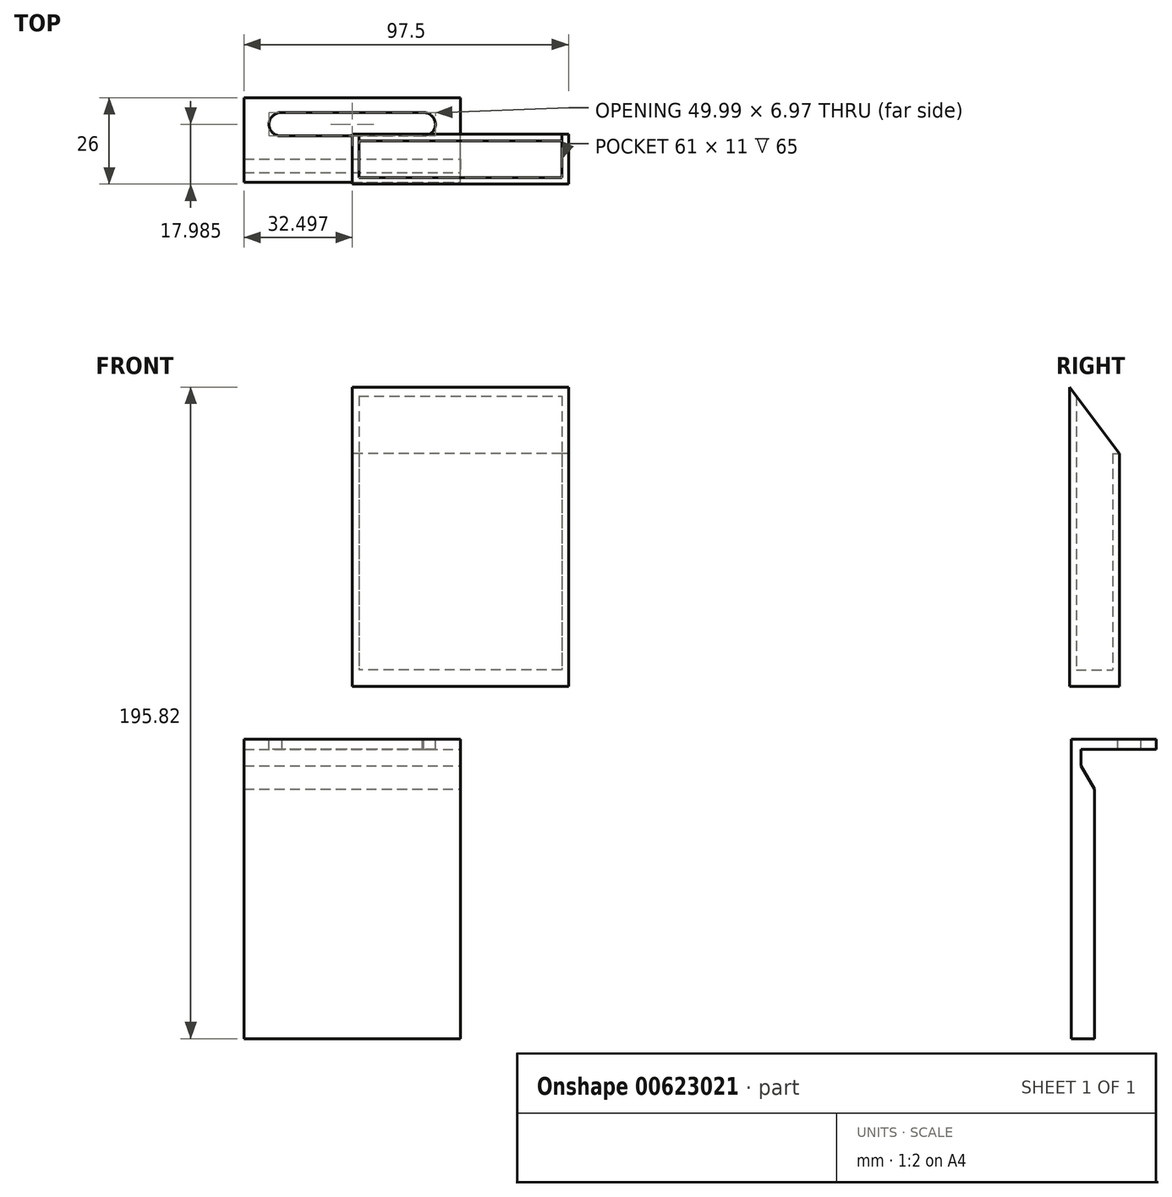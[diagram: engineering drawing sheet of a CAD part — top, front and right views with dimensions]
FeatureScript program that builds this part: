
annotation { "Feature Type Name" : "Feature", "Feature Type Description" : "" }
export const myFeature = defineFeature(function(context is Context, id is Id, definition is map)
    precondition{}
    {
        {
            var Q0;
            Q0=qCreatedBy(makeId("Top.planeOp"),FACE);
            var sketch = newSketch(context, id + "F0", { "sketchPlane" : qUnion([Q0])});
            skLineSegment(sketch, "E0.bottom", {"start": v(32.5, -7.5) * mm, "end": v(-32.5, -7.5) * mm});
            skLineSegment(sketch, "E0.top", {"start": v(32.5, 7.5) * mm, "end": v(-32.5, 7.5) * mm});
            skLineSegment(sketch, "E0.left", {"start": v(32.5, -7.5) * mm, "end": v(32.5, 7.5) * mm});
            skLineSegment(sketch, "E0.right", {"start": v(-32.5, -7.5) * mm, "end": v(-32.5, 7.5) * mm});
            skPoint(sketch, "E0.middle", {"position": v(0, 0) * mm});
            skSolve(sketch);
        }
        {
            var Q0;
            Q0 = qSketchRegion(id + "F0", true);
            extrude(context, id + "F1", {"entities" : qUnion([Q0]), "depth" : 5 * mm, "offsetDistance" : 25 * mm});
        }
        {
            var Q0;
            Q0=makeQuery(id+"F1.opExtrude","CAP_FACE",FACE,{"disambiguationData":[OSD([sQuery(id+"F0.wireOp",EDGE,"E0.bottom"),sQuery(id+"F0.wireOp",EDGE,"E0.top"),sQuery(id+"F0.wireOp",EDGE,"E0.left"),sQuery(id+"F0.wireOp",EDGE,"E0.right")])],"isStart":false});
            var sketch = newSketch(context, id + "F2", { "sketchPlane" : qUnion([Q0])});
            skLineSegment(sketch, "E1.bottom", {"start": v(32.5, -7.5) * mm, "end": v(-32.5, -7.5) * mm});
            skLineSegment(sketch, "E1.top", {"start": v(32.5, 7.5) * mm, "end": v(-32.5, 7.5) * mm});
            skLineSegment(sketch, "E1.left", {"start": v(32.5, -7.5) * mm, "end": v(32.5, 7.5) * mm});
            skLineSegment(sketch, "E1.right", {"start": v(-32.5, -7.5) * mm, "end": v(-32.5, 7.5) * mm});
            skPoint(sketch, "E1.middle", {"position": v(0, 0) * mm});
            skLineSegment(sketch, "E2.bottom", {"start": v(30.5, -5.5) * mm, "end": v(-30.5, -5.5) * mm});
            skLineSegment(sketch, "E2.top", {"start": v(30.5, 5.5) * mm, "end": v(-30.5, 5.5) * mm});
            skLineSegment(sketch, "E2.left", {"start": v(30.5, -5.5) * mm, "end": v(30.5, 5.5) * mm});
            skLineSegment(sketch, "E2.right", {"start": v(-30.5, -5.5) * mm, "end": v(-30.5, 5.5) * mm});
            skSolve(sketch);
        }
        {
            var Q0;
            Q0=makeQuery(id+"F2.imprint","IMPRINT",FACE,{"disambiguationData":[TD([[makeQuery(id+"F2.imprint","IMPRINT",EDGE,{"derivedFrom":sQuery(id+"F2.wireOp",EDGE,"E1.bottom")}),-1.0]])]});
            extrude(context, id + "F3", {"entities" : qUnion([Q0]), "operationType" : NewBodyOperationType.ADD, "depth" : 65 * mm, "offsetDistance" : 25 * mm});
        }
        {
            var Q0;
            Q0=makeQuery(id+"F3.boolean.opBoolean","MERGE",FACE,{"derivedFrom":[makeQuery(id+"F1.opExtrude","SWEPT_FACE",FACE,{"disambiguationData":[OSD([sQuery(id+"F0.wireOp",EDGE,"E0.left")])]}),makeQuery(id+"F3.opExtrude","SWEPT_FACE",FACE,{"disambiguationData":[OSD([sQuery(id+"F2.wireOp",EDGE,"E1.left")])]})]});
            var sketch = newSketch(context, id + "F4", { "sketchPlane" : qUnion([Q0])});
            skLineSegment(sketch, "E3", {"start": v(-7.5, 70) * mm, "end": v(-7.5, 90) * mm});
            skLineSegment(sketch, "E4", {"start": v(-7.5, 90) * mm, "end": v(7.5, 70) * mm});
            skLineSegment(sketch, "E5", {"start": v(7.5, 70) * mm, "end": v(-7.5, 70) * mm});
            skSolve(sketch);
        }
        {
            var Q0;
            Q0 = qSketchRegion(id + "F4", true);
            extrude(context, id + "F5", {"entities" : qUnion([Q0]), "operationType" : NewBodyOperationType.ADD, "oppositeDirection" : true, "depth" : 2 * mm, "offsetDistance" : 25 * mm});
        }
        {
            var Q0;
            Q0=makeQuery(id+"F3.boolean.opBoolean","MERGE",FACE,{"derivedFrom":[makeQuery(id+"F1.opExtrude","SWEPT_FACE",FACE,{"disambiguationData":[OSD([sQuery(id+"F0.wireOp",EDGE,"E0.right")])]}),makeQuery(id+"F3.opExtrude","SWEPT_FACE",FACE,{"disambiguationData":[OSD([sQuery(id+"F2.wireOp",EDGE,"E1.right")])]})]});
            var sketch = newSketch(context, id + "F6", { "sketchPlane" : qUnion([Q0])});
            skLineSegment(sketch, "E6", {"start": v(7.5, 70) * mm, "end": v(7.5, 90) * mm});
            skLineSegment(sketch, "E7", {"start": v(7.5, 90) * mm, "end": v(-7.5, 70) * mm});
            skLineSegment(sketch, "E8", {"start": v(-7.5, 70) * mm, "end": v(7.5, 70) * mm});
            skSolve(sketch);
        }
        {
            var Q0;
            Q0 = qSketchRegion(id + "F6", true);
            extrude(context, id + "F7", {"entities" : qUnion([Q0]), "operationType" : NewBodyOperationType.ADD, "oppositeDirection" : true, "depth" : 2 * mm, "offsetDistance" : 25 * mm});
        }
        {
            var Q0;
            {var subQ0=sQuery(id+"F2.wireOp",EDGE,"E2.left");var subQ1=sQuery(id+"F2.wireOp",EDGE,"E2.bottom");var subQ2=sQuery(id+"F2.wireOp",EDGE,"E1.bottom");var subQ4=sQuery(id+"F2.wireOp",EDGE,"E2.right");Q0=makeQuery(id+"F7.boolean.opBoolean","SPLIT",FACE,{"disambiguationData":[TD([makeQuery(id+"F1.opExtrude","SWEPT_FACE",FACE,{"disambiguationData":[OSD([sQuery(id+"F0.wireOp",EDGE,"E0.bottom")])]})])],"derivedFrom":makeQuery(id+"F3.opExtrude","CAP_FACE",FACE,{"disambiguationData":[OSD([subQ2,sQuery(id+"F2.wireOp",EDGE,"E1.top"),sQuery(id+"F2.wireOp",EDGE,"E1.left"),sQuery(id+"F2.wireOp",EDGE,"E1.right"),subQ1,sQuery(id+"F2.wireOp",EDGE,"E2.top"),subQ0,subQ4])],"isStart":false})});}
            var sketch = newSketch(context, id + "F8", { "sketchPlane" : qUnion([Q0])});
            skLineSegment(sketch, "E9", {"start": v(-30.5, -5.5) * mm, "end": v(30.5, -5.5) * mm});
            skLineSegment(sketch, "E10", {"start": v(30.5, -5.5) * mm, "end": v(30.5, -7.5) * mm});
            skLineSegment(sketch, "E11", {"start": v(30.5, -7.5) * mm, "end": v(-30.5, -7.5) * mm});
            skLineSegment(sketch, "E12", {"start": v(-30.5, -7.5) * mm, "end": v(-30.5, -5.5) * mm});
            skSolve(sketch);
        }
        {
            var Q0;
            Q0 = qSketchRegion(id + "F8", true);
            extrude(context, id + "F9", {"entities" : qUnion([Q0]), "operationType" : NewBodyOperationType.ADD, "depth" : 20 * mm, "offsetDistance" : 25 * mm});
        }
        {
            var Q0;
            Q0=makeQuery(id+"F9.opExtrude","SWEPT_FACE",FACE,{"disambiguationData":[OSD([sQuery(id+"F8.wireOp",EDGE,"E10")])]});
            extrude(context, id + "F10", {"entities" : qUnion([Q0]), "operationType" : NewBodyOperationType.REMOVE, "endBound" : BoundingType.THROUGH_ALL, "oppositeDirection" : true, "depth" : 25 * mm, "offsetDistance" : 25 * mm});
        }
        {
            var Q0;
            Q0=qCreatedBy(makeId("Right.planeOp"),FACE);
            var sketch = newSketch(context, id + "F11", { "sketchPlane" : qUnion([Q0])});
            skLineSegment(sketch, "E13", {"start": v(-7, -15.82) * mm, "end": v(-7, -105.82) * mm});
            skLineSegment(sketch, "E14", {"start": v(-7, -105.82) * mm, "end": v(0, -105.82) * mm});
            skLineSegment(sketch, "E15", {"start": v(0, -105.82) * mm, "end": v(0, -30.82) * mm});
            skLineSegment(sketch, "E16", {"start": v(0, -30.82) * mm, "end": v(-4, -23.82) * mm});
            skLineSegment(sketch, "E17", {"start": v(-4, -23.82) * mm, "end": v(-4, -18.82) * mm});
            skLineSegment(sketch, "E18", {"start": v(-4, -18.82) * mm, "end": v(18.5, -18.82) * mm});
            skLineSegment(sketch, "E19", {"start": v(-7, -15.82) * mm, "end": v(18.5, -15.82) * mm});
            skLineSegment(sketch, "E20", {"start": v(18.5, -15.82) * mm, "end": v(18.5, -18.82) * mm});
            skSolve(sketch);
        }
        {
            var Q0;
            Q0=makeQuery(id+"F11.imprint","IMPRINT",FACE,{"disambiguationData":[TD([[makeQuery(id+"F11.imprint","IMPRINT",EDGE,{"derivedFrom":sQuery(id+"F11.wireOp",EDGE,"E13")}),1.0]])]});
            extrude(context, id + "F12", {"entities" : qUnion([Q0]), "oppositeDirection" : true, "depth" : 65 * mm, "offsetDistance" : 25 * mm});
        }
        {
            var Q0;
            Q0=makeQuery(id+"F12.opExtrude","SWEPT_FACE",FACE,{"disambiguationData":[OSD([sQuery(id+"F11.wireOp",EDGE,"E19")])]});
            var sketch = newSketch(context, id + "F13", { "sketchPlane" : qUnion([Q0])});
            skPoint(sketch, "E21", {"position": v(-54, 10.5) * mm});
            skPoint(sketch, "E22", {"position": v(-11, 10.5) * mm});
            skSolve(sketch);
        }
        {
            var Q0;
            Q0=sQuery(id+"F13.wireOp",VERTEX,"E21");
            var Q1;
            Q1=sQuery(id+"F13.wireOp",VERTEX,"E22");
            var Q2;
            Q2=makeQuery(id+"F12.opExtrude","SWEPT_BODY",BODY,{"disambiguationData":[OSD([sQuery(id+"F11.wireOp",EDGE,"E13"),sQuery(id+"F11.wireOp",EDGE,"E14"),sQuery(id+"F11.wireOp",EDGE,"E15"),sQuery(id+"F11.wireOp",EDGE,"E16"),sQuery(id+"F11.wireOp",EDGE,"E17"),sQuery(id+"F11.wireOp",EDGE,"E18"),sQuery(id+"F11.wireOp",EDGE,"E19"),sQuery(id+"F11.wireOp",EDGE,"E20")])]});
            hole(context, id + "F14", {"style" : HoleStyle.SIMPLE, "endStyle" : HoleEndStyle.THROUGH, "holeDiameter" : 7 * mm, "majorDiameter" : 5 * mm, "isTappedThrough" : true, "tappedDepth" : 12 * mm, "tapClearance" : 3, "locations" : qUnion([Q0, Q1]), "scope" : qUnion([Q2])});
        }
        {
            var Q0;
            Q0=makeQuery(id+"F12.opExtrude","SWEPT_FACE",FACE,{"disambiguationData":[OSD([sQuery(id+"F11.wireOp",EDGE,"E19")])]});
            var sketch = newSketch(context, id + "F15", { "sketchPlane" : qUnion([Q0])});
            skLineSegment(sketch, "E23.bottom", {"start": v(-53.54, 13.97) * mm, "end": v(-11.06, 13.97) * mm});
            skLineSegment(sketch, "E23.top", {"start": v(-53.54, 7) * mm, "end": v(-11.06, 7) * mm});
            skLineSegment(sketch, "E23.left", {"start": v(-53.54, 13.97) * mm, "end": v(-53.54, 7) * mm});
            skLineSegment(sketch, "E23.right", {"start": v(-11.06, 13.97) * mm, "end": v(-11.06, 7) * mm});
            skSolve(sketch);
        }
        {
            var Q0;
            Q0 = qSketchRegion(id + "F15", true);
            extrude(context, id + "F16", {"entities" : qUnion([Q0]), "operationType" : NewBodyOperationType.REMOVE, "endBound" : BoundingType.THROUGH_ALL, "oppositeDirection" : true, "depth" : 25 * mm, "offsetDistance" : 25 * mm});
        }
    });
